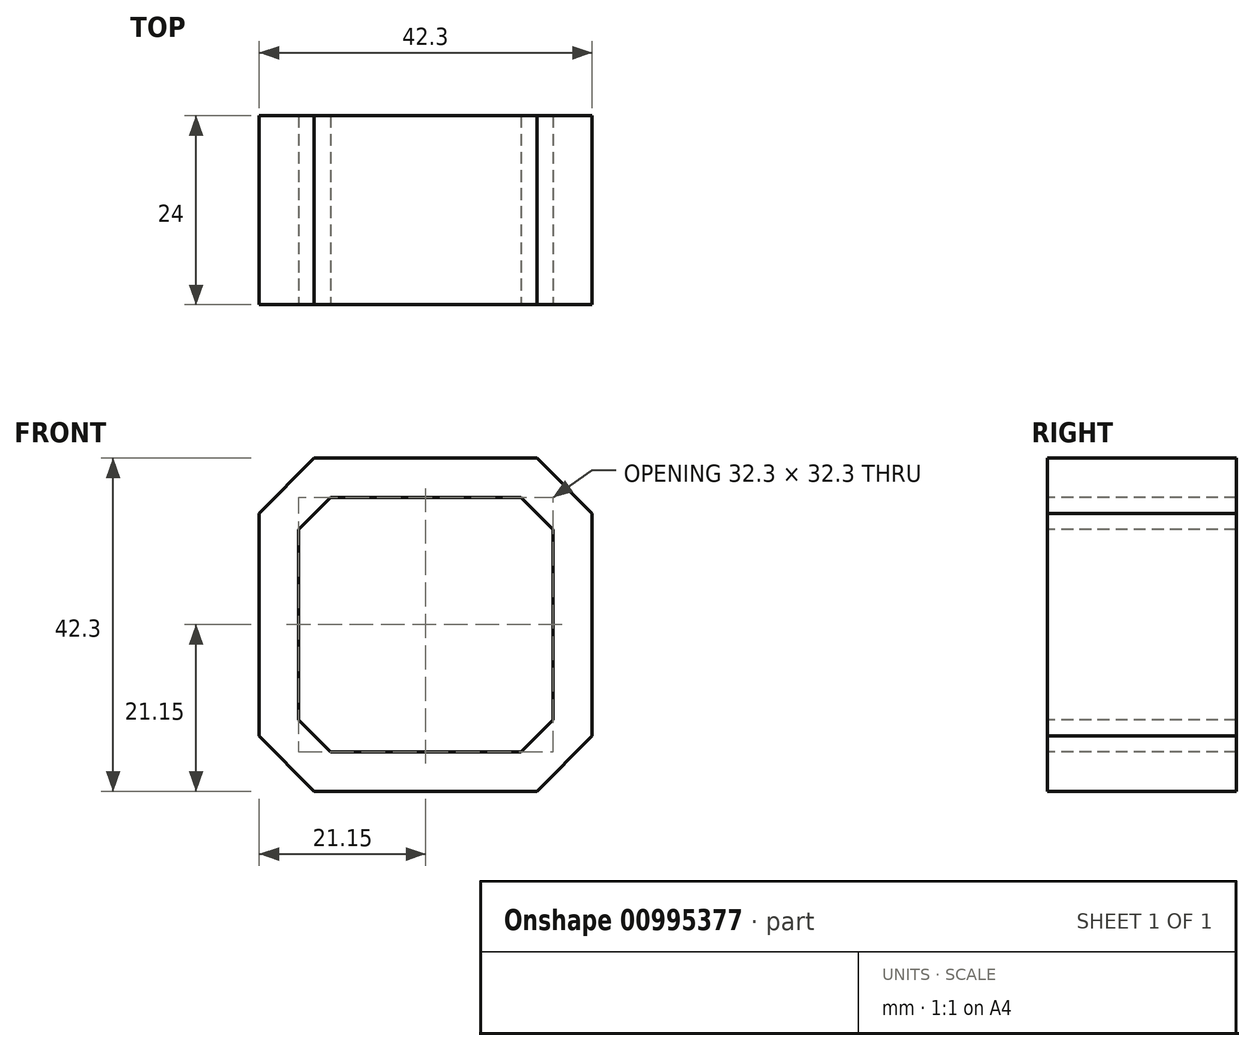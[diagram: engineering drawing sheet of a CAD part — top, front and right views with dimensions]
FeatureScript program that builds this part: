
annotation { "Feature Type Name" : "Feature", "Feature Type Description" : "" }
export const myFeature = defineFeature(function(context is Context, id is Id, definition is map)
    precondition{}
    {
        {
            var Q0;
            Q0=qCreatedBy(makeId("Front.planeOp"),FACE);
            var sketch = newSketch(context, id + "F0", { "sketchPlane" : qUnion([Q0])});
            skLineSegment(sketch, "E0.bottom", {"start": v(14.15, 21.15) * mm, "end": v(-14.15, 21.15) * mm});
            skLineSegment(sketch, "E0.top", {"start": v(14.15, -21.15) * mm, "end": v(-14.15, -21.15) * mm});
            skLineSegment(sketch, "E0.left", {"start": v(21.15, 14.15) * mm, "end": v(21.15, -14.15) * mm});
            skLineSegment(sketch, "E0.right", {"start": v(-21.15, 14.15) * mm, "end": v(-21.15, -14.15) * mm});
            skPoint(sketch, "E0.middle", {"position": v(0, 0) * mm});
            skLineSegment(sketch, "E1", {"start": v(14.15, 21.15) * mm, "end": v(21.15, 14.15) * mm});
            skLineSegment(sketch, "E2.1.0", {"start": v(-21.15, 14.15) * mm, "end": v(-14.15, 21.15) * mm});
            skLineSegment(sketch, "E2.2.0", {"start": v(-14.15, -21.15) * mm, "end": v(-21.15, -14.15) * mm});
            skLineSegment(sketch, "E2.3.0", {"start": v(21.15, -14.15) * mm, "end": v(14.15, -21.15) * mm});
            skPoint(sketch, "E3.orphan", {"position": v(-21.15, 21.15) * mm});
            skPoint(sketch, "E4.orphan", {"position": v(-21.15, -21.15) * mm});
            skPoint(sketch, "E5.orphan", {"position": v(21.15, -21.15) * mm});
            skPoint(sketch, "E6.orphan", {"position": v(21.15, 21.15) * mm});
            skSolve(sketch);
        }
        {
            var Q0;
            Q0=makeQuery(id+"F0.imprint","IMPRINT",FACE,{"disambiguationData":[TD([[makeQuery(id+"F0.imprint","IMPRINT",EDGE,{"derivedFrom":sQuery(id+"F0.wireOp",EDGE,"E0.bottom")}),1.0]])]});
            extrude(context, id + "F1", {"entities" : qUnion([Q0]), "depth" : 24 * mm, "offsetDistance" : 25 * mm});
        }
        {
            var Q0;
            Q0=makeQuery(id+"F1.opExtrude","CAP_FACE",FACE,{"disambiguationData":[OSD([sQuery(id+"F0.wireOp",EDGE,"E0.bottom"),sQuery(id+"F0.wireOp",EDGE,"E0.top"),sQuery(id+"F0.wireOp",EDGE,"E0.left"),sQuery(id+"F0.wireOp",EDGE,"E0.right"),sQuery(id+"F0.wireOp",EDGE,"E1"),sQuery(id+"F0.wireOp",EDGE,"E2.1.0"),sQuery(id+"F0.wireOp",EDGE,"E2.2.0"),sQuery(id+"F0.wireOp",EDGE,"E2.3.0")])],"isStart":false});
            var sketch = newSketch(context, id + "F2", { "sketchPlane" : qUnion([Q0])});
            skLineSegment(sketch, "E7.0", {"start": v(16.15, -12.08) * mm, "end": v(12.08, -16.15) * mm});
            skLineSegment(sketch, "E7.1", {"start": v(16.15, 12.08) * mm, "end": v(16.15, -12.08) * mm});
            skLineSegment(sketch, "E7.2", {"start": v(12.08, -16.15) * mm, "end": v(-12.08, -16.15) * mm});
            skLineSegment(sketch, "E7.3", {"start": v(12.08, 16.15) * mm, "end": v(16.15, 12.08) * mm});
            skLineSegment(sketch, "E7.4", {"start": v(-12.08, -16.15) * mm, "end": v(-16.15, -12.08) * mm});
            skLineSegment(sketch, "E7.5", {"start": v(-16.15, 12.08) * mm, "end": v(-16.15, -12.08) * mm});
            skLineSegment(sketch, "E7.6", {"start": v(-16.15, 12.08) * mm, "end": v(-12.08, 16.15) * mm});
            skLineSegment(sketch, "E7.7", {"start": v(12.08, 16.15) * mm, "end": v(-12.08, 16.15) * mm});
            skSolve(sketch);
        }
        {
            var Q0;
            Q0 = qSketchRegion(id + "F2", true);
            extrude(context, id + "F3", {"entities" : qUnion([Q0]), "operationType" : NewBodyOperationType.REMOVE, "endBound" : BoundingType.THROUGH_ALL, "oppositeDirection" : true, "depth" : 25 * mm, "offsetDistance" : 25 * mm});
        }
    });
